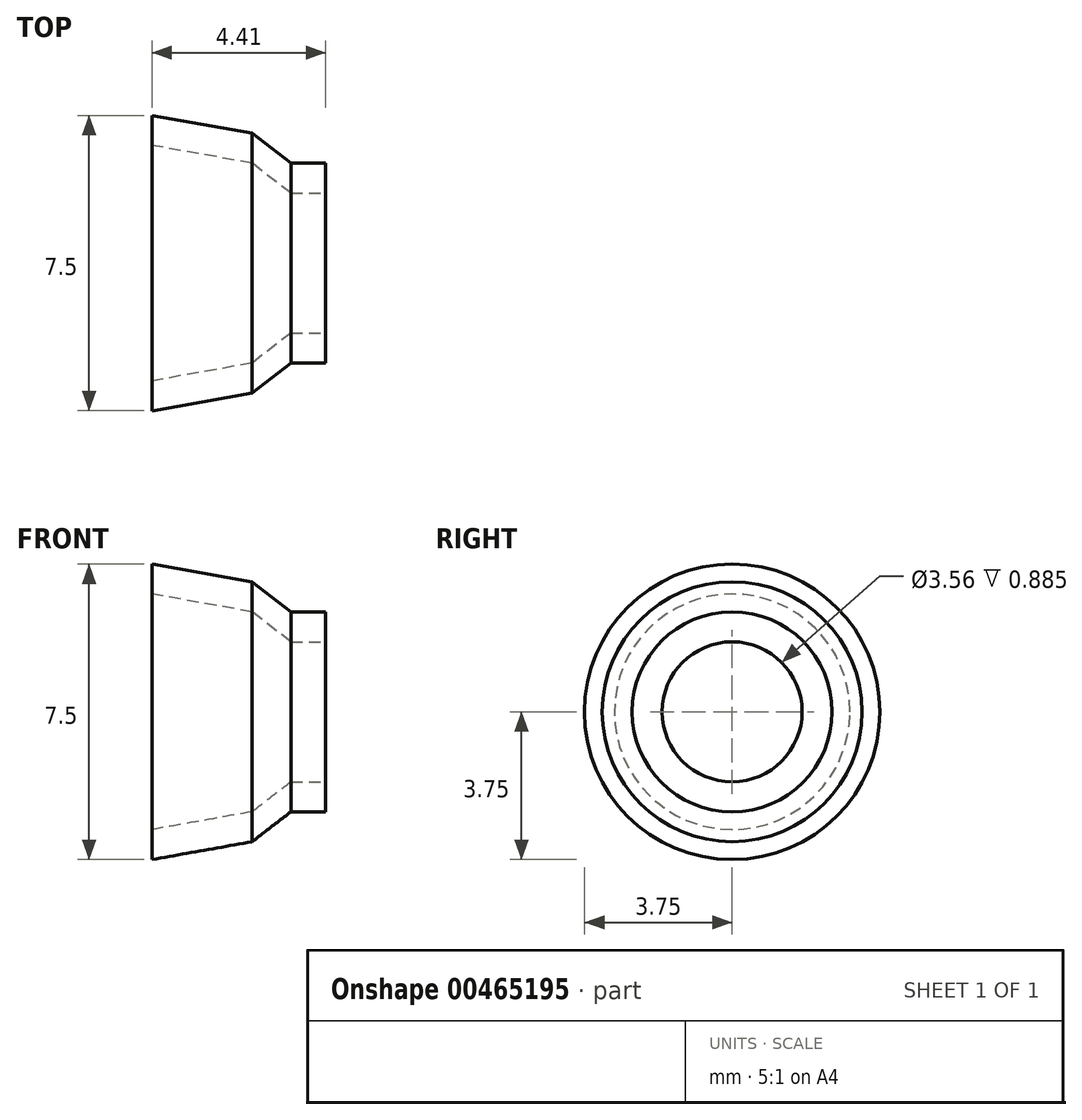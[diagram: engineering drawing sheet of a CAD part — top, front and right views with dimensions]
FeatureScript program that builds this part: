
annotation { "Feature Type Name" : "Feature", "Feature Type Description" : "" }
export const myFeature = defineFeature(function(context is Context, id is Id, definition is map)
    precondition{}
    {
        {
            var Q0;
            Q0=qCreatedBy(makeId("Top.planeOp"),FACE);
            var sketch = newSketch(context, id + "F0", { "sketchPlane" : qUnion([Q0])});
            skLineSegment(sketch, "E0", {"start": v(-4.41, 3) * mm, "end": v(-4.41, 3.75) * mm});
            skLineSegment(sketch, "E1", {"start": v(-4.41, 3.75) * mm, "end": v(-1.87, 3.3) * mm});
            skLineSegment(sketch, "E2", {"start": v(-1.87, 3.3) * mm, "end": v(-0.88, 2.54) * mm});
            skLineSegment(sketch, "E3", {"start": v(-0.88, 2.54) * mm, "end": v(0, 2.54) * mm});
            skLineSegment(sketch, "E4", {"start": v(0, 2.54) * mm, "end": v(0, 1.78) * mm});
            skLineSegment(sketch, "E5", {"start": v(0, 1.78) * mm, "end": v(-0.88, 1.78) * mm});
            skLineSegment(sketch, "E6", {"start": v(-0.88, 1.78) * mm, "end": v(-1.87, 2.54) * mm});
            skLineSegment(sketch, "E7", {"start": v(-1.87, 2.54) * mm, "end": v(-4.41, 3) * mm});
            skLineSegment(sketch, "E8", {"start": v(0, 0) * mm, "end": v(-7.63, 0) * mm});
            skSolve(sketch);
        }
        {
            var Q0;
            Q0=makeQuery(id+"F0.imprint","IMPRINT",FACE,{"disambiguationData":[TD([[makeQuery(id+"F0.imprint","IMPRINT",EDGE,{"derivedFrom":sQuery(id+"F0.wireOp",EDGE,"E0")}),-1.0]])]});
            var Q1;
            Q1=sQuery(id+"F0.wireOp",EDGE,"E8");
            revolve(context, id + "F1", {"entities" : qUnion([Q0]), "axis" : qUnion([Q1]), "revolveType" : RevolveType.FULL});
        }
    });
